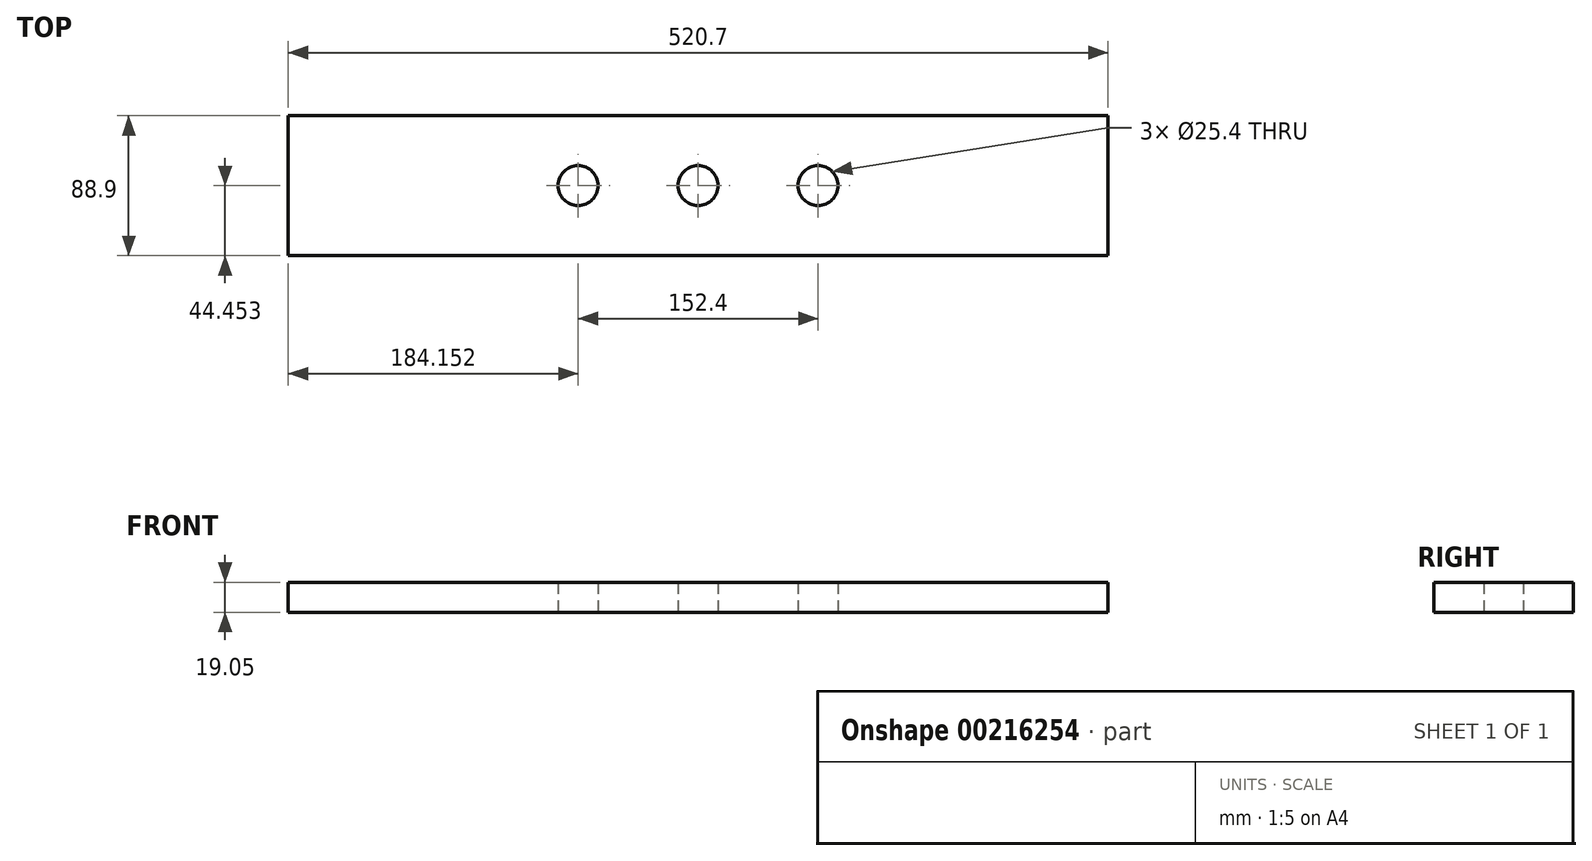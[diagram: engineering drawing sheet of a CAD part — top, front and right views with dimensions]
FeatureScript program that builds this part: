
annotation { "Feature Type Name" : "Feature", "Feature Type Description" : "" }
export const myFeature = defineFeature(function(context is Context, id is Id, definition is map)
    precondition{}
    {
        {
            var Q0;
            Q0=qCreatedBy(makeId("Top.planeOp"),FACE);
            var sketch = newSketch(context, id + "F0", { "sketchPlane" : qUnion([Q0])});
            skLineSegment(sketch, "E0", {"start": v(-1767.74, -2625.4) * mm, "end": v(-1247.04, -2625.4) * mm});
            skLineSegment(sketch, "E1", {"start": v(-1247.04, -2625.4) * mm, "end": v(-1247.04, -2536.5) * mm});
            skLineSegment(sketch, "E2", {"start": v(-1247.04, -2536.5) * mm, "end": v(-1767.74, -2536.5) * mm});
            skLineSegment(sketch, "E3", {"start": v(-1767.74, -2536.5) * mm, "end": v(-1767.74, -2625.4) * mm});
            skCircle(sketch, "E4", {"center": v(-1507.39, -2580.96) * mm, "radius": 12.7 * mm});
            skCircle(sketch, "E5", {"center": v(-1431.19, -2580.96) * mm, "radius": 12.7 * mm});
            skCircle(sketch, "E6", {"center": v(-1583.59, -2580.96) * mm, "radius": 12.7 * mm});
            skSolve(sketch);
        }
        {
            var Q0;
            Q0=makeQuery(id+"F0.imprint","IMPRINT",FACE,{"disambiguationData":[TD([[makeQuery(id+"F0.imprint","IMPRINT",EDGE,{"derivedFrom":sQuery(id+"F0.wireOp",EDGE,"E0")}),1.0]])]});
            extrude(context, id + "F1", {"entities" : qUnion([Q0]), "depth" : 19.05 * mm});
        }
    });
